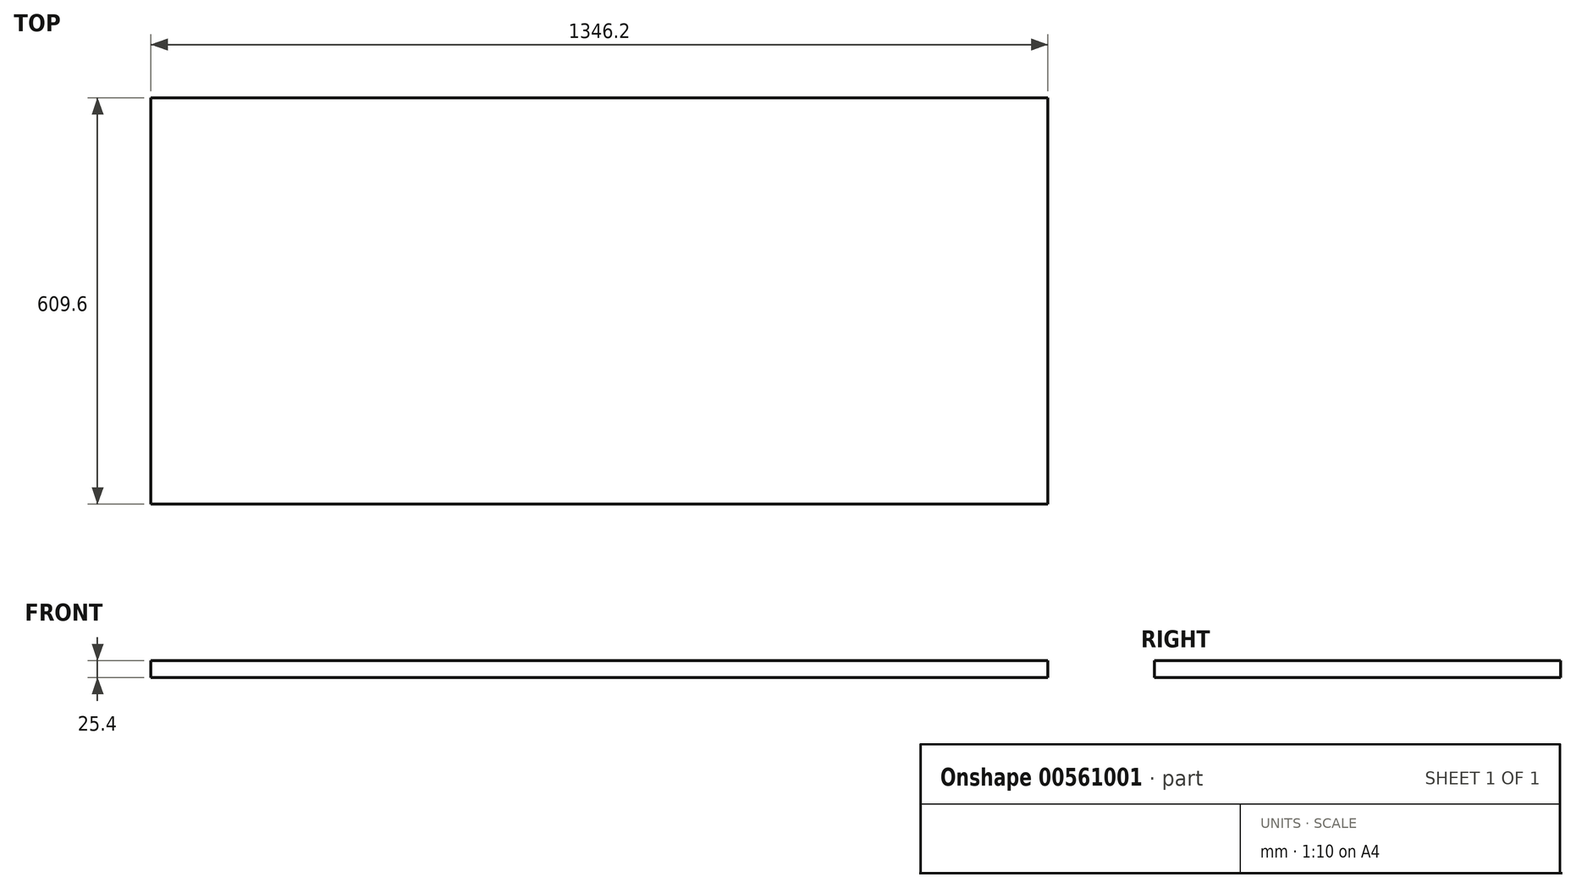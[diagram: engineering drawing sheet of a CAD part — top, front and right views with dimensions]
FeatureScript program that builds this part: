
annotation { "Feature Type Name" : "Feature", "Feature Type Description" : "" }
export const myFeature = defineFeature(function(context is Context, id is Id, definition is map)
    precondition{}
    {
        {
            var Q0;
            Q0=qCreatedBy(makeId("Top.planeOp"),FACE);
            var sketch = newSketch(context, id + "F0", { "sketchPlane" : qUnion([Q0])});
            skLineSegment(sketch, "E0.bottom", {"start": v(-673.1, 304.8) * mm, "end": v(673.1, 304.8) * mm});
            skLineSegment(sketch, "E0.top", {"start": v(-673.1, -304.8) * mm, "end": v(673.1, -304.8) * mm});
            skLineSegment(sketch, "E0.left", {"start": v(-673.1, 304.8) * mm, "end": v(-673.1, -304.8) * mm});
            skLineSegment(sketch, "E0.right", {"start": v(673.1, 304.8) * mm, "end": v(673.1, -304.8) * mm});
            skLineSegment(sketch, "E1", {"start": v(673.1, 304.8) * mm, "end": v(-673.1, -304.8) * mm, "construction": true});
            skSolve(sketch);
        }
        {
            var Q0;
            Q0=makeQuery(id+"F0.imprint","IMPRINT",FACE,{"disambiguationData":[TD([[makeQuery(id+"F0.imprint","IMPRINT",EDGE,{"derivedFrom":sQuery(id+"F0.wireOp",EDGE,"E0.bottom")}),-1.0]])]});
            extrude(context, id + "F1", {"entities" : qUnion([Q0]), "depth" : 25.4 * mm, "offsetDistance" : 25.4 * mm});
        }
    });
